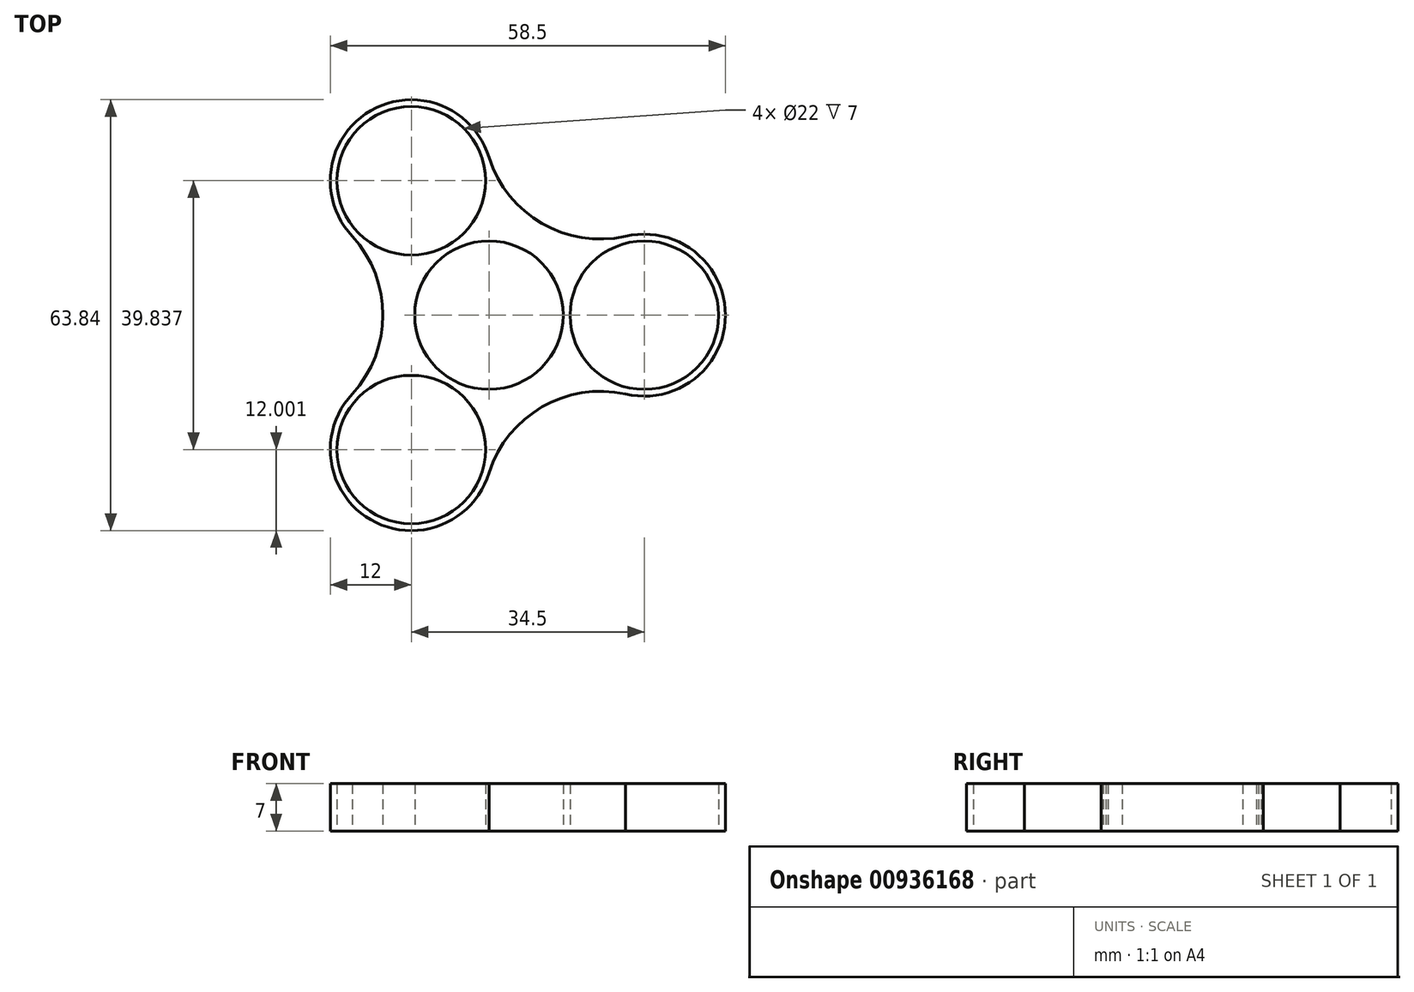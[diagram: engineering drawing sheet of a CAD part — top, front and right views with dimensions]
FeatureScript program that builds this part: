
annotation { "Feature Type Name" : "Feature", "Feature Type Description" : "" }
export const myFeature = defineFeature(function(context is Context, id is Id, definition is map)
    precondition{}
    {
        {
            var Q0;
            Q0=qCreatedBy(makeId("Top.planeOp"),FACE);
            var sketch = newSketch(context, id + "F0", { "sketchPlane" : qUnion([Q0])});
            skCircle(sketch, "E0", {"center": v(0, 0) * mm, "radius": 11 * mm});
            skCircle(sketch, "E1", {"center": v(0, 0) * mm, "radius": 12 * mm});
            skCircle(sketch, "E2", {"center": v(23, 0) * mm, "radius": 11 * mm});
            skArc(sketch, "E3", {"start": v(11.5, -3.43) * mm, "mid": v(35, 0) * mm, "end": v(11.5, 3.43) * mm});
            skArc(sketch, "E4.1.0", {"start": v(-2.78, 11.67) * mm, "mid": v(-17.5, 30.31) * mm, "end": v(-8.72, 8.25) * mm});
            skCircle(sketch, "E4.1.1", {"center": v(-11.5, 19.92) * mm, "radius": 11 * mm});
            skArc(sketch, "E4.2.0", {"start": v(-8.72, -8.25) * mm, "mid": v(-17.5, -30.31) * mm, "end": v(-2.78, -11.67) * mm});
            skCircle(sketch, "E4.2.1", {"center": v(-11.5, -19.92) * mm, "radius": 11 * mm});
            skArc(sketch, "E5", {"start": v(20.22, -11.67) * mm, "mid": v(7.85, -13.6) * mm, "end": v(0, -23.35) * mm});
            skArc(sketch, "E6.1.0", {"start": v(0, 23.35) * mm, "mid": v(7.85, 13.6) * mm, "end": v(20.22, 11.67) * mm});
            skArc(sketch, "E6.2.0", {"start": v(-20.22, -11.67) * mm, "mid": v(-15.7, 0) * mm, "end": v(-20.22, 11.67) * mm});
            skSolve(sketch);
        }
        {
            var Q0;
            Q0 = qSketchRegion(id + "F0", true);
            var Q1;
            Q1=makeQuery(id+"F0.imprint","IMPRINT",FACE,{"disambiguationData":[TD([[makeQuery(id+"F0.imprint","IMPRINT",EDGE,{"derivedFrom":sQuery(id+"F0.wireOp",EDGE,"E0")}),-1.0]])]});
            extrude(context, id + "F1", {"entities" : qUnion([Q0, Q1]), "depth" : 7 * mm, "offsetDistance" : 25 * mm});
        }
    });
